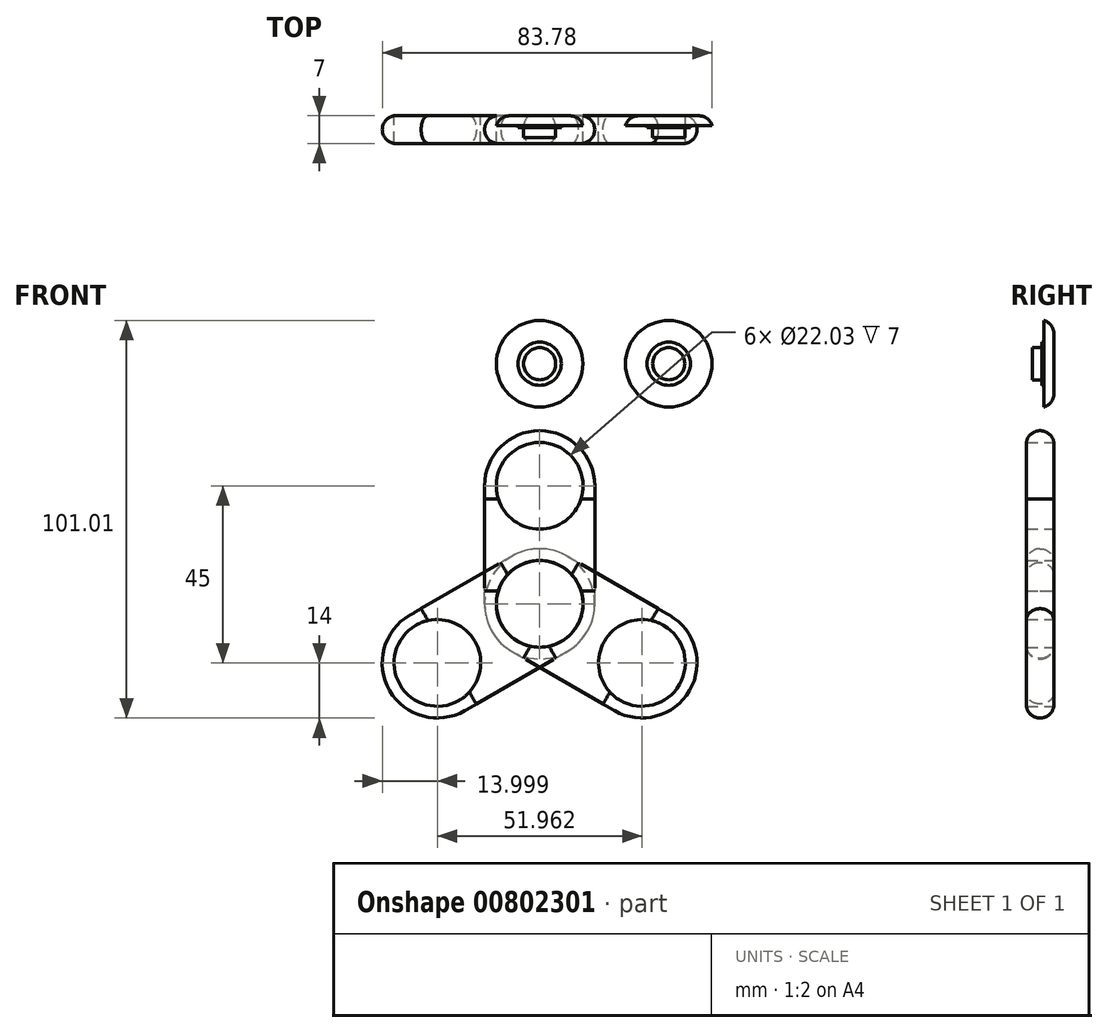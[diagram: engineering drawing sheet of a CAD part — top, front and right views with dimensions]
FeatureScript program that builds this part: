
annotation { "Feature Type Name" : "Feature", "Feature Type Description" : "" }
export const myFeature = defineFeature(function(context is Context, id is Id, definition is map)
    precondition{}
    {
        {
            var Q0;
            Q0=qCreatedBy(makeId("Front.planeOp"),FACE);
            var sketch = newSketch(context, id + "F0", { "sketchPlane" : qUnion([Q0])});
            skLineSegment(sketch, "E0", {"start": v(0, 0) * mm, "end": v(-14, 0) * mm});
            skLineSegment(sketch, "E1", {"start": v(-14, 0) * mm, "end": v(-14, 30) * mm});
            skLineSegment(sketch, "E2", {"start": v(-14, 30) * mm, "end": v(0, 30) * mm});
            skLineSegment(sketch, "E3", {"start": v(0, 30) * mm, "end": v(14, 30) * mm});
            skLineSegment(sketch, "E4", {"start": v(14, 30) * mm, "end": v(14, 0) * mm});
            skLineSegment(sketch, "E5", {"start": v(14, 0) * mm, "end": v(0, 0) * mm});
            skCircle(sketch, "E6", {"center": v(0, 30) * mm, "radius": 14 * mm});
            skCircle(sketch, "E7", {"center": v(0, 30) * mm, "radius": 11.02 * mm});
            skCircle(sketch, "E8", {"center": v(0, 0) * mm, "radius": 14 * mm});
            skCircle(sketch, "E9", {"center": v(0, 0) * mm, "radius": 11.02 * mm});
            skSolve(sketch);
        }
        {
            var Q0;
            {var subQ0=sQuery(id+"F0.wireOp",EDGE,"E1");Q0=makeQuery(id+"F0.imprint","IMPRINT",FACE,{"disambiguationData":[TD([[makeQuery(id+"F0.imprint","IMPRINT",EDGE,{"derivedFrom":subQ0}),-1.0]])]});}
            var Q1;
            {var subQ1=sQuery(id+"F0.wireOp",EDGE,"E2");var subQ3=sQuery(id+"F0.wireOp",EDGE,"E7");var subQ4=makeQuery(id+"F0.imprint","INTERSECT",VERTEX,{"derivedFrom":[subQ1,subQ3]});Q1=makeQuery(id+"F0.imprint","IMPRINT",FACE,{"disambiguationData":[TD([[makeQuery(id+"F0.imprint","IMPRINT",EDGE,{"disambiguationData":[TD([[subQ4,-1.0]])],"derivedFrom":subQ3}),-1.0]])]});}
            var Q2;
            {var subQ1=sQuery(id+"F0.wireOp",EDGE,"E2");var subQ3=sQuery(id+"F0.wireOp",EDGE,"E7");var subQ4=makeQuery(id+"F0.imprint","INTERSECT",VERTEX,{"derivedFrom":[subQ1,subQ3]});Q2=makeQuery(id+"F0.imprint","IMPRINT",FACE,{"disambiguationData":[TD([[makeQuery(id+"F0.imprint","IMPRINT",EDGE,{"disambiguationData":[TD([[subQ4,1.0]])],"derivedFrom":subQ3}),-1.0]])]});}
            var Q3;
            {var subQ1=sQuery(id+"F0.wireOp",EDGE,"E0");var subQ3=sQuery(id+"F0.wireOp",EDGE,"E9");var subQ4=makeQuery(id+"F0.imprint","INTERSECT",VERTEX,{"derivedFrom":[subQ1,subQ3]});Q3=makeQuery(id+"F0.imprint","IMPRINT",FACE,{"disambiguationData":[TD([[makeQuery(id+"F0.imprint","IMPRINT",EDGE,{"disambiguationData":[TD([[subQ4,1.0]])],"derivedFrom":subQ3}),-1.0]])]});}
            var Q4;
            {var subQ1=sQuery(id+"F0.wireOp",EDGE,"E0");var subQ3=sQuery(id+"F0.wireOp",EDGE,"E9");var subQ4=makeQuery(id+"F0.imprint","INTERSECT",VERTEX,{"derivedFrom":[subQ1,subQ3]});Q4=makeQuery(id+"F0.imprint","IMPRINT",FACE,{"disambiguationData":[TD([[makeQuery(id+"F0.imprint","IMPRINT",EDGE,{"disambiguationData":[TD([[subQ4,-1.0]])],"derivedFrom":subQ3}),-1.0]])]});}
            extrude(context, id + "F1", {"entities" : qUnion([Q0, Q1, Q2, Q3, Q4]), "depth" : 7 * mm, "offsetDistance" : 25 * mm});
        }
        {
            var Q0;
            Q0=makeQuery(id+"F1.opExtrude","SWEPT_BODY",BODY,{"disambiguationData":[OSD([sQuery(id+"F0.wireOp",EDGE,"E1"),sQuery(id+"F0.wireOp",EDGE,"E4"),sQuery(id+"F0.wireOp",EDGE,"E6"),sQuery(id+"F0.wireOp",EDGE,"E7"),sQuery(id+"F0.wireOp",EDGE,"E8"),sQuery(id+"F0.wireOp",EDGE,"E9")])]});
            var Q1;
            Q1=makeQuery(id+"F1.opExtrude","SWEPT_FACE",FACE,{"disambiguationData":[OSD([sQuery(id+"F0.wireOp",EDGE,"E8")])]});
            circularPattern(context, id + "F2", {"entities" : qUnion([Q0]), "axis" : qUnion([Q1]), "angle" : 360 * degree, "instanceCount" : 3, "equalSpace" : true});
        }
        {
            var Q0;
            Q0=qCreatedBy(makeId("Front.planeOp"),FACE);
            var sketch = newSketch(context, id + "F3", { "sketchPlane" : qUnion([Q0])});
            skCircle(sketch, "E10", {"center": v(0, 61.01) * mm, "radius": 11 * mm});
            skCircle(sketch, "E11", {"center": v(0, 61.01) * mm, "radius": 5.5 * mm});
            skCircle(sketch, "E12", {"center": v(0, 61.01) * mm, "radius": 4.08 * mm});
            skSolve(sketch);
        }
        {
            var Q0;
            Q0=makeQuery(id+"F3.imprint","IMPRINT",FACE,{"disambiguationData":[TD([[makeQuery(id+"F3.imprint","IMPRINT",EDGE,{"derivedFrom":sQuery(id+"F3.wireOp",EDGE,"E10")}),1.0]])]});
            extrude(context, id + "F4", {"entities" : qUnion([Q0]), "depth" : 2.5 * mm, "offsetDistance" : 25 * mm});
        }
        {
            var Q0;
            Q0=makeQuery(id+"F3.imprint","IMPRINT",FACE,{"disambiguationData":[TD([[makeQuery(id+"F3.imprint","IMPRINT",EDGE,{"derivedFrom":sQuery(id+"F3.wireOp",EDGE,"E11")}),1.0]])]});
            extrude(context, id + "F5", {"entities" : qUnion([Q0]), "operationType" : NewBodyOperationType.ADD, "depth" : 3 * mm, "offsetDistance" : 25 * mm});
        }
        {
            var Q0;
            Q0=makeQuery(id+"F3.imprint","IMPRINT",FACE,{"disambiguationData":[TD([[makeQuery(id+"F3.imprint","IMPRINT",EDGE,{"derivedFrom":sQuery(id+"F3.wireOp",EDGE,"E12")}),1.0]])]});
            extrude(context, id + "F6", {"entities" : qUnion([Q0]), "operationType" : NewBodyOperationType.ADD, "depth" : 5.5 * mm, "offsetDistance" : 25 * mm});
        }
        {
            var Q0;
            Q0=makeQuery(id+"F2.opPattern","COPY",EDGE,{"derivedFrom":makeQuery(id+"F1.opExtrude","CAP_EDGE",EDGE,{"disambiguationData":[OSD([sQuery(id+"F0.wireOp",EDGE,"E1")])],"isStart":false}),"instanceName":"2"});
            var Q1;
            Q1=makeQuery(id+"F2.opPattern","COPY",EDGE,{"derivedFrom":makeQuery(id+"F1.opExtrude","CAP_EDGE",EDGE,{"disambiguationData":[OSD([sQuery(id+"F0.wireOp",EDGE,"E4")])],"isStart":false}),"instanceName":"1"});
            var Q2;
            Q2=makeQuery(id+"F1.opExtrude","CAP_EDGE",EDGE,{"disambiguationData":[OSD([sQuery(id+"F0.wireOp",EDGE,"E4")])],"isStart":false});
            var Q3;
            Q3=makeQuery(id+"F1.opExtrude","CAP_EDGE",EDGE,{"disambiguationData":[OSD([sQuery(id+"F0.wireOp",EDGE,"E1")])],"isStart":true});
            var Q4;
            Q4=makeQuery(id+"F2.opPattern","COPY",EDGE,{"derivedFrom":makeQuery(id+"F1.opExtrude","CAP_EDGE",EDGE,{"disambiguationData":[OSD([sQuery(id+"F0.wireOp",EDGE,"E4")])],"isStart":true}),"instanceName":"2"});
            var Q5;
            Q5=makeQuery(id+"F1.opExtrude","CAP_EDGE",EDGE,{"disambiguationData":[OSD([sQuery(id+"F0.wireOp",EDGE,"E4")])],"isStart":true});
            var Q6;
            Q6=makeQuery(id+"F2.opPattern","COPY",EDGE,{"derivedFrom":makeQuery(id+"F1.opExtrude","CAP_EDGE",EDGE,{"disambiguationData":[OSD([sQuery(id+"F0.wireOp",EDGE,"E1")])],"isStart":true}),"instanceName":"1"});
            var Q7;
            Q7=makeQuery(id+"F2.opPattern","COPY",EDGE,{"derivedFrom":makeQuery(id+"F1.opExtrude","CAP_EDGE",EDGE,{"disambiguationData":[OSD([sQuery(id+"F0.wireOp",EDGE,"E4")])],"isStart":true}),"instanceName":"1"});
            var Q8;
            Q8=makeQuery(id+"F2.opPattern","COPY",EDGE,{"derivedFrom":makeQuery(id+"F1.opExtrude","CAP_EDGE",EDGE,{"disambiguationData":[OSD([sQuery(id+"F0.wireOp",EDGE,"E6")])],"isStart":true}),"instanceName":"1"});
            var Q9;
            Q9=makeQuery(id+"F2.opPattern","COPY",EDGE,{"derivedFrom":makeQuery(id+"F1.opExtrude","CAP_EDGE",EDGE,{"disambiguationData":[OSD([sQuery(id+"F0.wireOp",EDGE,"E6")])],"isStart":true}),"instanceName":"2"});
            var Q10;
            Q10=makeQuery(id+"F1.opExtrude","CAP_EDGE",EDGE,{"disambiguationData":[OSD([sQuery(id+"F0.wireOp",EDGE,"E6")])],"isStart":true});
            var Q11;
            Q11=makeQuery(id+"F1.opExtrude","CAP_EDGE",EDGE,{"disambiguationData":[OSD([sQuery(id+"F0.wireOp",EDGE,"E6")])],"isStart":false});
            var Q12;
            Q12=makeQuery(id+"F2.opPattern","COPY",EDGE,{"derivedFrom":makeQuery(id+"F1.opExtrude","CAP_EDGE",EDGE,{"disambiguationData":[OSD([sQuery(id+"F0.wireOp",EDGE,"E6")])],"isStart":false}),"instanceName":"2"});
            var Q13;
            Q13=makeQuery(id+"F2.opPattern","COPY",EDGE,{"derivedFrom":makeQuery(id+"F1.opExtrude","CAP_EDGE",EDGE,{"disambiguationData":[OSD([sQuery(id+"F0.wireOp",EDGE,"E1")])],"isStart":false}),"instanceName":"1"});
            var Q14;
            Q14=makeQuery(id+"F2.opPattern","COPY",EDGE,{"derivedFrom":makeQuery(id+"F1.opExtrude","CAP_EDGE",EDGE,{"disambiguationData":[OSD([sQuery(id+"F0.wireOp",EDGE,"E6")])],"isStart":false}),"instanceName":"1"});
            var Q15;
            Q15=makeQuery(id+"F1.opExtrude","CAP_EDGE",EDGE,{"disambiguationData":[OSD([sQuery(id+"F0.wireOp",EDGE,"E1")])],"isStart":false});
            var Q16;
            Q16=makeQuery(id+"F4.opExtrude","CAP_EDGE",EDGE,{"disambiguationData":[OSD([sQuery(id+"F3.wireOp",EDGE,"E10")])],"isStart":true});
            fillet(context, id + "F7", {"entities" : qUnion([Q0, Q1, Q2, Q3, Q4, Q5, Q6, Q7, Q8, Q9, Q10, Q11, Q12, Q13, Q14, Q15, Q16]), "radius" : 3.5 * mm, "tangentPropagation" : true, "allowEdgeOverflow" : false});
        }
        {
            var Q0;
            Q0=makeQuery(id+"F4.opExtrude","SWEPT_BODY",BODY,{"disambiguationData":[OSD([sQuery(id+"F3.wireOp",EDGE,"E10"),sQuery(id+"F3.wireOp",EDGE,"E11")])]});
            transform(context, id + "F8", {"entities" : qUnion([Q0]), "transformType" : TransformType.TRANSLATION_3D, "dx" : 32.8 * mm, "dy" : 0 * mm, "dz" : 0 * mm, "makeCopy" : true});
        }
    });
